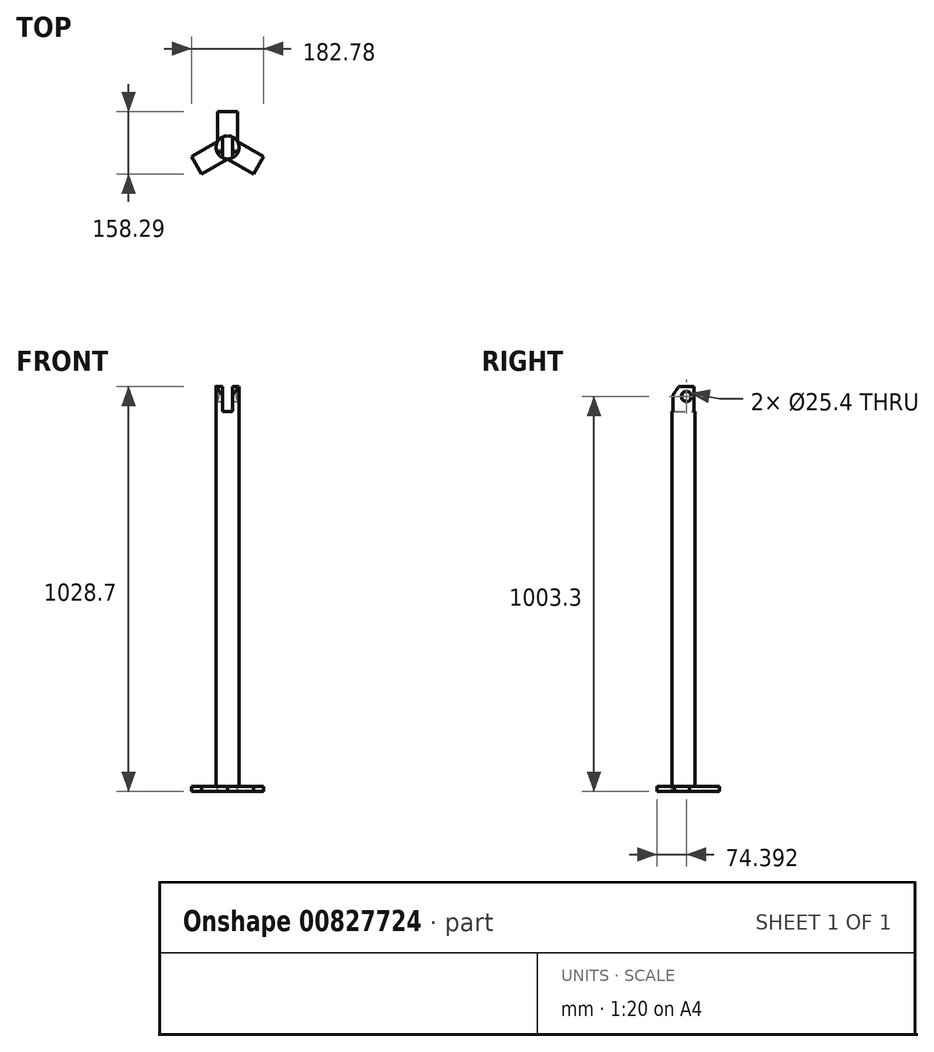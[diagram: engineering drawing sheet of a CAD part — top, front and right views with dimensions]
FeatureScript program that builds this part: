
annotation { "Feature Type Name" : "Feature", "Feature Type Description" : "" }
export const myFeature = defineFeature(function(context is Context, id is Id, definition is map)
    precondition{}
    {
        {
            var Q0;
            Q0=qCreatedBy(makeId("Top.planeOp"),FACE);
            var sketch = newSketch(context, id + "F0", { "sketchPlane" : qUnion([Q0])});
            skPoint(sketch, "E0.middle", {"position": v(0, 0) * mm});
            skLineSegment(sketch, "E1.0", {"start": v(-25.4, 29.33) * mm, "end": v(25.4, 29.33) * mm, "construction": true});
            skLineSegment(sketch, "E1.1", {"start": v(25.4, 29.33) * mm, "end": v(0, -14.66) * mm, "construction": true});
            skLineSegment(sketch, "E1.2", {"start": v(0, -14.66) * mm, "end": v(-25.4, 29.33) * mm, "construction": true});
            skPoint(sketch, "E1.0.midPoint", {"position": v(0, 29.33) * mm});
            skLineSegment(sketch, "E2", {"start": v(-25.4, 29.33) * mm, "end": v(-91.4, -8.77) * mm});
            skLineSegment(sketch, "E3", {"start": v(-91.4, -8.77) * mm, "end": v(-66, -52.76) * mm});
            skLineSegment(sketch, "E4", {"start": v(-66, -52.76) * mm, "end": v(0, -14.66) * mm});
            skLineSegment(sketch, "E5.top", {"start": v(-25.4, 105.53) * mm, "end": v(25.4, 105.53) * mm});
            skLineSegment(sketch, "E5.left", {"start": v(-25.4, 29.33) * mm, "end": v(-25.4, 105.53) * mm});
            skLineSegment(sketch, "E6", {"start": v(0, -14.66) * mm, "end": v(66, -52.76) * mm});
            skLineSegment(sketch, "E7", {"start": v(66, -52.76) * mm, "end": v(91.4, -8.77) * mm});
            skLineSegment(sketch, "E8", {"start": v(91.4, -8.77) * mm, "end": v(25.4, 29.33) * mm});
            skLineSegment(sketch, "E9", {"start": v(25.4, 29.33) * mm, "end": v(25.4, 105.53) * mm});
            skSolve(sketch);
        }
        {
            var Q0;
            Q0=qSketchRegion(id+"F0",true);
            extrude(context, id + "F1", {"entities" : qUnion([Q0]), "oppositeDirection" : true, "depth" : 12.7 * mm, "offsetDistance" : 25.4 * mm});
        }
        {
            var Q0;
            Q0=makeQuery(id+"F1.opExtrude","CAP_FACE",FACE,{"disambiguationData":[OSD([sQuery(id+"F0.wireOp",EDGE,"E2"),sQuery(id+"F0.wireOp",EDGE,"E3"),sQuery(id+"F0.wireOp",EDGE,"E4"),sQuery(id+"F0.wireOp",EDGE,"E5.top"),sQuery(id+"F0.wireOp",EDGE,"E5.left"),sQuery(id+"F0.wireOp",EDGE,"E5.right"),sQuery(id+"F0.wireOp",EDGE,"E6"),sQuery(id+"F0.wireOp",EDGE,"E7"),sQuery(id+"F0.wireOp",EDGE,"E8")])],"isStart":true});
            var sketch = newSketch(context, id + "F2", { "sketchPlane" : qUnion([Q0])});
            skCircle(sketch, "E10", {"center": v(0, 14.66) * mm, "radius": 29.33 * mm});
            skPoint(sketch, "E10.first.point", {"position": v(-25.4, 29.33) * mm});
            skPoint(sketch, "E10.second.point", {"position": v(0, -14.66) * mm});
            skPoint(sketch, "E10.third.point", {"position": v(25.4, 29.33) * mm});
            skSolve(sketch);
        }
        {
            var Q0;
            Q0=qSketchRegion(id+"F2",true);
            extrude(context, id + "F3", {"entities" : qUnion([Q0]), "operationType" : NewBodyOperationType.ADD, "depth" : 1016 * mm, "offsetDistance" : 25.4 * mm});
        }
        {
            var Q0;
            Q0=makeQuery(id+"F3.opExtrude","CAP_FACE",FACE,{"disambiguationData":[OSD([sQuery(id+"F2.wireOp",EDGE,"E10")])],"isStart":false});
            var sketch = newSketch(context, id + "F4", { "sketchPlane" : qUnion([Q0])});
            skLineSegment(sketch, "E11.bottom", {"start": v(12.7, -17.09) * mm, "end": v(-12.7, -17.09) * mm});
            skLineSegment(sketch, "E11.top", {"start": v(12.7, 46.41) * mm, "end": v(-12.7, 46.41) * mm});
            skLineSegment(sketch, "E11.left", {"start": v(12.7, -17.09) * mm, "end": v(12.7, 46.41) * mm});
            skLineSegment(sketch, "E11.right", {"start": v(-12.7, -17.09) * mm, "end": v(-12.7, 46.41) * mm});
            skPoint(sketch, "E11.middle", {"position": v(0, 14.66) * mm});
            skSolve(sketch);
        }
        {
            var Q0;
            Q0=qSketchRegion(id+"F4",true);
            extrude(context, id + "F5", {"entities" : qUnion([Q0]), "operationType" : NewBodyOperationType.REMOVE, "oppositeDirection" : true, "depth" : 63.5 * mm, "offsetDistance" : 25.4 * mm});
        }
        {
            var Q0;
            Q0=makeQuery(id+"F5.boolean.opBoolean","COPY",FACE,{"derivedFrom":makeQuery(id+"F5.opExtrude","SWEPT_FACE",FACE,{"disambiguationData":[OSD([sQuery(id+"F4.wireOp",EDGE,"E11.right")])]})});
            var sketch = newSketch(context, id + "F6", { "sketchPlane" : qUnion([Q0])});
            skLineSegment(sketch, "E12.0", {"start": v(-11.77, 1016) * mm, "end": v(-11.77, 994.76) * mm});
            skLineSegment(sketch, "E13.0", {"start": v(-11.77, 1016) * mm, "end": v(2.16, 1016) * mm});
            skLineSegment(sketch, "E14", {"start": v(-11.77, 994.76) * mm, "end": v(2.16, 1016) * mm});
            skPoint(sketch, "E15.orphan", {"position": v(41.1, 1016) * mm});
            skPoint(sketch, "E16.orphan", {"position": v(-11.77, 952.5) * mm});
            skSolve(sketch);
        }
        {
            var Q0;
            Q0=qSketchRegion(id+"F6",true);
            extrude(context, id + "F7", {"entities" : qUnion([Q0]), "operationType" : NewBodyOperationType.REMOVE, "oppositeDirection" : true, "depth" : 25.4 * mm, "offsetDistance" : 25.4 * mm, "hasSecondDirection" : true, "secondDirectionOppositeDirection" : false, "secondDirectionDepth" : 127 * mm});
        }
        {
            var Q0;
            Q0=makeQuery(id+"F5.boolean.opBoolean","COPY",FACE,{"derivedFrom":makeQuery(id+"F5.opExtrude","SWEPT_FACE",FACE,{"disambiguationData":[OSD([sQuery(id+"F4.wireOp",EDGE,"E11.right")])]})});
            var sketch = newSketch(context, id + "F8", { "sketchPlane" : qUnion([Q0])});
            skCircle(sketch, "E17", {"center": v(21.63, 990.6) * mm, "radius": 12.7 * mm});
            skPoint(sketch, "E17.centerSnap0", {"position": v(21.63, 1016) * mm});
            skSolve(sketch);
        }
        {
            var Q0;
            Q0=qSketchRegion(id+"F8",true);
            extrude(context, id + "F9", {"entities" : qUnion([Q0]), "operationType" : NewBodyOperationType.REMOVE, "oppositeDirection" : true, "depth" : 25.4 * mm, "offsetDistance" : 25.4 * mm, "hasSecondDirection" : true, "secondDirectionOppositeDirection" : false, "secondDirectionDepth" : 127 * mm});
        }
    });
